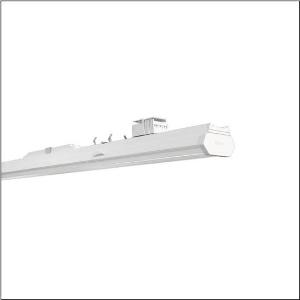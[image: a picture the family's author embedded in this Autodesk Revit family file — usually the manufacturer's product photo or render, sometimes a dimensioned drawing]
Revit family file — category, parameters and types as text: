
# Revit family: licross_r__21_protected_mo_52td12dne75f_b15f
name_source: partatom
category: Lighting Fixtures
units: mm (PartAtom-declared; Revit-internal decimal feet)

## family parameters
Cut with Voids When Loaded = No
Host = Face
Light Source = No
Part Type = Normal
Room Calculation Point = No
Round Connector Dimension = Use Diameter
Shared = No

## types (1)
- --- (1 x LED, 7720 lm, 61 W, 5000K)
    Apparent Load = 61 VA
    CIE Flux Codes = 73 92 98 99 100
    Color Rendering = 90
    Color Temperature = 5000K
    Default Elevation = 1800 mm
    Description = Licross® 21 Protected MO, luminaire insert, of sheet steel, galvanised, coil coated, white, length: 1.500mm, width: 90mm, height: 103mm, LED rated luminous flux: 7.720lm, light colour: 950, control gear: DALI 2, control gear: ECG DALI, with plug, 5-pole, with phase selection, mains connection: 220..240V, AC, 50/60Hz, rated input power: 61W, halogen-free wiring, primary optical cover: cover, of PMMA, light emission: direct distribution, primary light characteristic: symmetric, protection rating (complete): IP54, insulation class (complete): insulation class I (protective earthing), certification: CE, ENEC, VDE, UKCA, protection symbol: D if used in an environment with non-conductive dust loads with corresponding accessories, impact resistance: IK06, permissible ambient temperature for indoor applications: -25..+40°C, corresponds to IFS (International Featured Standards) requirements for safety and quality in the food industry, reducing of maximum allowable ambient temperature of 5°C with ceiling mounting, LABS conformity tested according to VDMA 24364:2018-05, packaging unit: 1 piece
    Height = 92 mm
    Lamp = 1 x LED
    Lamp Light Flux = 7720 lm
    Lamp Power = 61 W
    Lamp count = 1
    Length = 1500 mm
    Luminous efficacy = 127 lm/W
    Manufacturer = Siteco
    ModVariant = No
    Model = 52TD12DNE75F
    Mounting Place = Ceiling
    Mounting Type = Pendant
    Number of Poles = 1
    OnlyDefault = Yes
    Power Factor = 1
    Product Name = Licross® 21 Protected MO
    Product group = luminaire insert
    ProductGroupID = 901
    Protection Class = Protection class I
    Protection Degree = IP 54
    RLX_Detail_Level = 1
    RLX_Emergency_Light_Flux = 0 lm
    RLX_Emergency_Type = 0
    RLX_Emergency_Type_DB = No
    RlxData = <blob elided: 24389 chars, md5=7c66a3c2>
    Socket = socket
    Standby Power = 0 W
    System Light Flux = 7720 lm
    System Power = 61 W
    Type Comments = factory setting: luminous flux: 100 % | dim-lin: 254 | 405 mA
    Type Image = l_1256148.jpg
    URL = http://relux.com
    VarID = @adj_136359
    Voltage = 0 V
    Weight = 0.00 kg
    Width = 88 mm

## geometry (parser evidence)
native form markers: Blend x4, Sweep x10
no freeform markers — native parametric forms only
